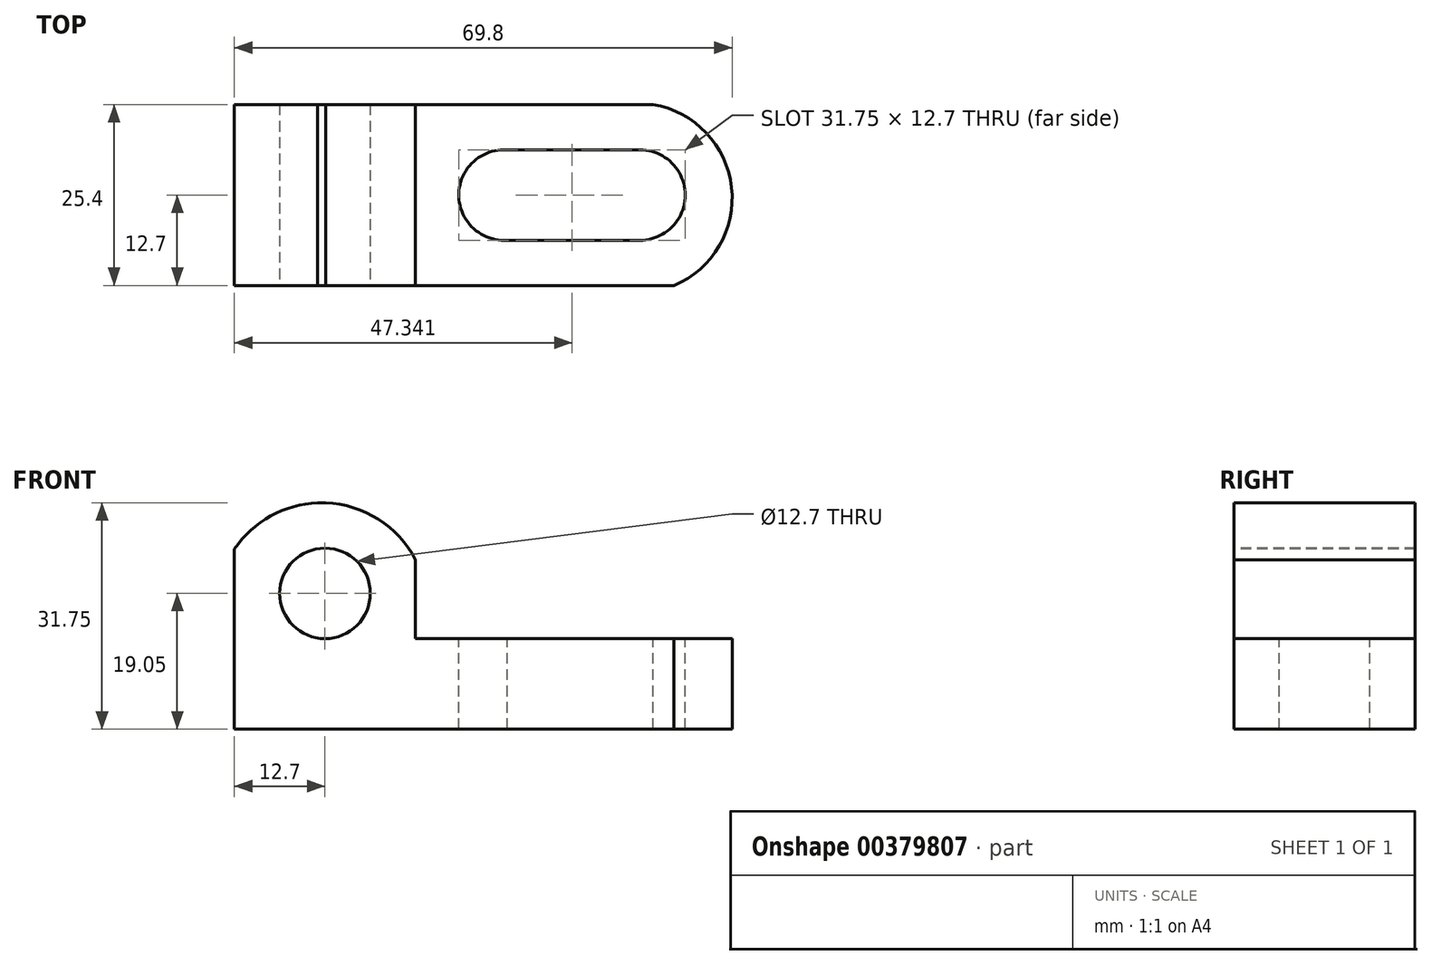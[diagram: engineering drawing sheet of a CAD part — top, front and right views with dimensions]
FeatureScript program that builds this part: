
annotation { "Feature Type Name" : "Feature", "Feature Type Description" : "" }
export const myFeature = defineFeature(function(context is Context, id is Id, definition is map)
    precondition{}
    {
        {
            var Q0;
            Q0=qCreatedBy(makeId("Front.planeOp"),FACE);
            var sketch = newSketch(context, id + "F0", { "sketchPlane" : qUnion([Q0])});
            skLineSegment(sketch, "E0", {"start": v(0, 0) * mm, "end": v(0, 31.75) * mm});
            skLineSegment(sketch, "E1", {"start": v(0, 31.75) * mm, "end": v(25.4, 31.75) * mm});
            skLineSegment(sketch, "E2", {"start": v(25.4, 31.75) * mm, "end": v(25.4, 12.7) * mm});
            skLineSegment(sketch, "E3", {"start": v(25.4, 12.7) * mm, "end": v(69.85, 12.7) * mm});
            skLineSegment(sketch, "E4", {"start": v(69.85, 12.7) * mm, "end": v(69.85, 0) * mm});
            skLineSegment(sketch, "E5", {"start": v(69.85, 0) * mm, "end": v(0, 0) * mm});
            skSolve(sketch);
        }
        {
            var Q0;
            Q0=makeQuery(id+"F0.imprint","IMPRINT",FACE,{"disambiguationData":[TD([[makeQuery(id+"F0.imprint","IMPRINT",EDGE,{"derivedFrom":sQuery(id+"F0.wireOp",EDGE,"E0")}),-1.0]])]});
            var sketch = newSketch(context, id + "F1", { "sketchPlane" : qUnion([Q0])});
            skSolve(sketch);
        }
        {
            var Q0;
            Q0 = qSketchRegion(id + "F1", true);
            var Q1;
            Q1=makeQuery(id+"F0.imprint","IMPRINT",FACE,{"disambiguationData":[TD([[makeQuery(id+"F0.imprint","IMPRINT",EDGE,{"derivedFrom":sQuery(id+"F0.wireOp",EDGE,"E0")}),-1.0]])]});
            extrude(context, id + "F2", {"entities" : qUnion([Q0, Q1]), "depth" : 25.4 * mm});
        }
        {
            var Q0;
            Q0=makeQuery(id+"F2.opExtrude","CAP_FACE",FACE,{"disambiguationData":[OSD([sQuery(id+"F0.wireOp",EDGE,"E0"),sQuery(id+"F0.wireOp",EDGE,"E1"),sQuery(id+"F0.wireOp",EDGE,"E2"),sQuery(id+"F0.wireOp",EDGE,"E3"),sQuery(id+"F0.wireOp",EDGE,"E4"),sQuery(id+"F0.wireOp",EDGE,"E5")])],"isStart":false});
            var sketch = newSketch(context, id + "F3", { "sketchPlane" : qUnion([Q0])});
            skCircle(sketch, "E6", {"center": v(12.7, 19.05) * mm, "radius": 6.35 * mm});
            skSolve(sketch);
        }
        {
            var Q0;
            Q0=makeQuery(id+"F3.imprint","IMPRINT",FACE,{"disambiguationData":[TD([[makeQuery(id+"F3.imprint","IMPRINT",EDGE,{"derivedFrom":sQuery(id+"F3.wireOp",EDGE,"E6")}),1.0]])]});
            extrude(context, id + "F4", {"entities" : qUnion([Q0]), "operationType" : NewBodyOperationType.REMOVE, "oppositeDirection" : true, "depth" : 25.4 * mm});
        }
        {
            var Q0;
            Q0=makeQuery(id+"F2.opExtrude","CAP_FACE",FACE,{"disambiguationData":[OSD([sQuery(id+"F0.wireOp",EDGE,"E0"),sQuery(id+"F0.wireOp",EDGE,"E1"),sQuery(id+"F0.wireOp",EDGE,"E2"),sQuery(id+"F0.wireOp",EDGE,"E3"),sQuery(id+"F0.wireOp",EDGE,"E4"),sQuery(id+"F0.wireOp",EDGE,"E5")])],"isStart":false});
            var sketch = newSketch(context, id + "F5", { "sketchPlane" : qUnion([Q0])});
            skArc(sketch, "E7", {"start": v(25.4, 23.74) * mm, "mid": v(13.14, 31.73) * mm, "end": v(0, 25.27) * mm});
            skSolve(sketch);
        }
        {
            var Q0;
            {var subQ0=sQuery(id+"F5.wireOp",EDGE,"E7");var subQ1=makeQuery(id+"F2.opExtrude","CAP_EDGE",EDGE,{"disambiguationData":[OSD([sQuery(id+"F0.wireOp",EDGE,"E2")])],"isStart":false});var subQ2=makeQuery(id+"F5.imprint","INTERSECT",VERTEX,{"derivedFrom":[subQ1,subQ0]});Q0=makeQuery(id+"F5.imprint","IMPRINT",FACE,{"disambiguationData":[TD([[makeQuery(id+"F5.imprint","IMPRINT",EDGE,{"disambiguationData":[TD([[subQ2,-1.0]])],"derivedFrom":subQ0}),-1.0]])]});}
            var Q1;
            {var subQ0=sQuery(id+"F5.wireOp",EDGE,"E7");var subQ1=makeQuery(id+"F2.opExtrude","CAP_EDGE",EDGE,{"disambiguationData":[OSD([sQuery(id+"F0.wireOp",EDGE,"E0")])],"isStart":false});var subQ2=makeQuery(id+"F5.imprint","INTERSECT",VERTEX,{"derivedFrom":[subQ1,subQ0]});Q1=makeQuery(id+"F5.imprint","IMPRINT",FACE,{"disambiguationData":[TD([[makeQuery(id+"F5.imprint","IMPRINT",EDGE,{"disambiguationData":[TD([[subQ2,1.0]])],"derivedFrom":subQ0}),-1.0]])]});}
            extrude(context, id + "F6", {"entities" : qUnion([Q0, Q1]), "operationType" : NewBodyOperationType.ADD, "depth" : 25.4 * mm});
        }
        {
            var Q0;
            Q0=makeQuery(id+"F6.opExtrude","CAP_FACE",FACE,{"disambiguationData":[OSD([sQuery(id+"F0.wireOp",EDGE,"E0"),sQuery(id+"F0.wireOp",EDGE,"E1"),sQuery(id+"F5.wireOp",EDGE,"E7")])],"isStart":false});
            var sketch = newSketch(context, id + "F7", { "sketchPlane" : qUnion([Q0])});
            skSolve(sketch);
        }
        {
            var Q0;
            Q0=makeQuery(id+"F6.opExtrude","CAP_FACE",FACE,{"disambiguationData":[OSD([sQuery(id+"F0.wireOp",EDGE,"E1"),sQuery(id+"F0.wireOp",EDGE,"E2"),sQuery(id+"F5.wireOp",EDGE,"E7")])],"isStart":false});
            var Q1;
            {var subQ1=sQuery(id+"F0.wireOp",EDGE,"E0");Q1=makeQuery(id+"F7.imprint","IMPRINT",FACE,{"disambiguationData":[TD([[makeQuery(id+"F7.imprint","IMPRINT",EDGE,{"derivedFrom":makeQuery(id+"F6.opExtrude","CAP_EDGE",EDGE,{"disambiguationData":[OSD([subQ1])],"isStart":false})}),-1.0]])]});}
            extrude(context, id + "F8", {"entities" : qUnion([Q0, Q1]), "operationType" : NewBodyOperationType.REMOVE, "oppositeDirection" : true, "depth" : 50.8 * mm});
        }
        {
            var Q0;
            Q0=makeQuery(id+"F2.opExtrude","SWEPT_FACE",FACE,{"disambiguationData":[OSD([sQuery(id+"F0.wireOp",EDGE,"E3")])]});
            var sketch = newSketch(context, id + "F9", { "sketchPlane" : qUnion([Q0])});
            skArc(sketch, "E8", {"start": v(61.63, -25.4) * mm, "mid": v(69.71, -11.61) * mm, "end": v(58.73, 0) * mm});
            skSolve(sketch);
        }
        {
            var Q0;
            Q0 = qSketchRegion(id + "F9", true);
            var Q1;
            {var subQ0=sQuery(id+"F9.wireOp",EDGE,"E8");Q1=makeQuery(id+"F9.imprint","IMPRINT",FACE,{"disambiguationData":[TD([[makeQuery(id+"F9.imprint","IMPRINT",EDGE,{"derivedFrom":subQ0}),-1.0]])]});}
            extrude(context, id + "F10", {"entities" : qUnion([Q0, Q1]), "operationType" : NewBodyOperationType.REMOVE, "oppositeDirection" : true, "depth" : 25.4 * mm});
        }
        {
            var Q0;
            Q0=makeQuery(id+"F2.opExtrude","SWEPT_FACE",FACE,{"disambiguationData":[OSD([sQuery(id+"F0.wireOp",EDGE,"E3")])]});
            var sketch = newSketch(context, id + "F11", { "sketchPlane" : qUnion([Q0])});
            skCircle(sketch, "E9", {"center": v(37.81, -12.7) * mm, "radius": 6.35 * mm});
            skCircle(sketch, "E10", {"center": v(56.86, -12.7) * mm, "radius": 6.35 * mm});
            skSolve(sketch);
        }
        {
            var Q0;
            Q0=makeQuery(id+"F11.imprint","IMPRINT",FACE,{"disambiguationData":[TD([[makeQuery(id+"F11.imprint","IMPRINT",EDGE,{"derivedFrom":sQuery(id+"F11.wireOp",EDGE,"E10")}),1.0]])]});
            var Q1;
            Q1=makeQuery(id+"F11.imprint","IMPRINT",FACE,{"disambiguationData":[TD([[makeQuery(id+"F11.imprint","IMPRINT",EDGE,{"derivedFrom":sQuery(id+"F11.wireOp",EDGE,"E9")}),1.0]])]});
            extrude(context, id + "F12", {"entities" : qUnion([Q0, Q1]), "operationType" : NewBodyOperationType.REMOVE, "oppositeDirection" : true, "depth" : 25.4 * mm});
        }
        {
            var Q0;
            Q0=makeQuery(id+"F2.opExtrude","SWEPT_FACE",FACE,{"disambiguationData":[OSD([sQuery(id+"F0.wireOp",EDGE,"E3")])]});
            var sketch = newSketch(context, id + "F13", { "sketchPlane" : qUnion([Q0])});
            skLineSegment(sketch, "E11", {"start": v(38.23, -6.36) * mm, "end": v(56.86, -6.35) * mm});
            skLineSegment(sketch, "E12", {"start": v(37.8, -19.05) * mm, "end": v(56.86, -19.05) * mm});
            skSolve(sketch);
        }
        {
            var Q0;
            {var subQ0=sQuery(id+"F13.wireOp",EDGE,"E11");Q0=makeQuery(id+"F13.imprint","IMPRINT",FACE,{"disambiguationData":[TD([[makeQuery(id+"F13.imprint","IMPRINT",EDGE,{"derivedFrom":subQ0}),-1.0]])]});}
            var sketch = newSketch(context, id + "F14", { "sketchPlane" : qUnion([Q0])});
            skSolve(sketch);
        }
        {
            var Q0;
            Q0 = qSketchRegion(id + "F14", true);
            var Q1;
            {var subQ0=sQuery(id+"F13.wireOp",EDGE,"E11");Q1=makeQuery(id+"F13.imprint","IMPRINT",FACE,{"disambiguationData":[TD([[makeQuery(id+"F13.imprint","IMPRINT",EDGE,{"derivedFrom":subQ0}),-1.0]])]});}
            extrude(context, id + "F15", {"entities" : qUnion([Q0, Q1]), "operationType" : NewBodyOperationType.REMOVE, "oppositeDirection" : true, "depth" : 25.4 * mm});
        }
    });
